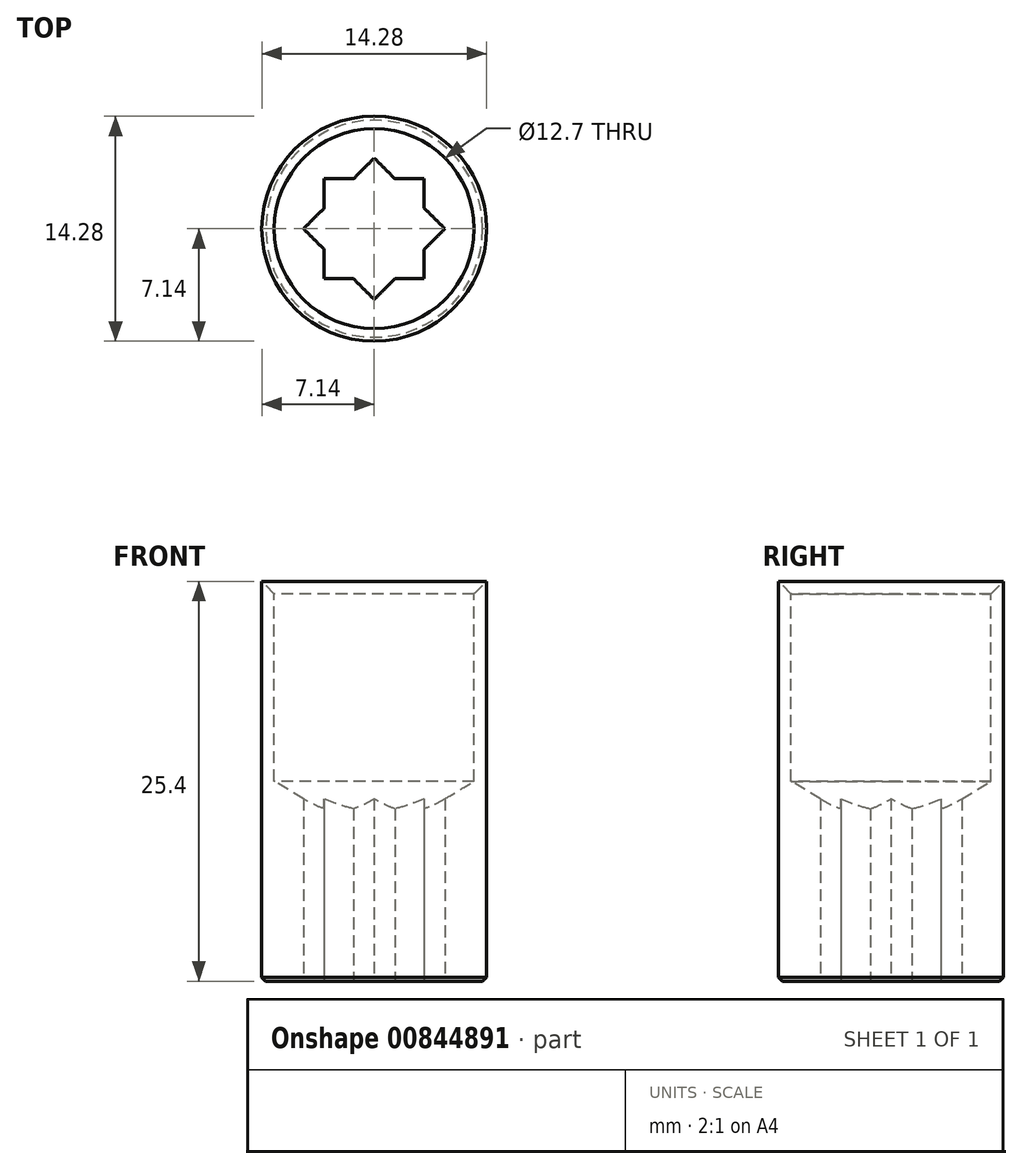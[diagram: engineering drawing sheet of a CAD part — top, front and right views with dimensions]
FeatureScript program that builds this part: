
annotation { "Feature Type Name" : "Feature", "Feature Type Description" : "" }
export const myFeature = defineFeature(function(context is Context, id is Id, definition is map)
    precondition{}
    {
        {
            var Q0;
            Q0=qCreatedBy(makeId("Front.planeOp"),FACE);
            var sketch = newSketch(context, id + "F0", { "sketchPlane" : qUnion([Q0])});
            skLineSegment(sketch, "E0.bottom", {"start": v(0, 0) * mm, "end": v(-7.14, 0) * mm});
            skLineSegment(sketch, "E0.top", {"start": v(0, -25.4) * mm, "end": v(-7.14, -25.4) * mm});
            skLineSegment(sketch, "E0.left", {"start": v(0, 0) * mm, "end": v(0, -25.4) * mm});
            skLineSegment(sketch, "E0.right", {"start": v(-7.14, 0) * mm, "end": v(-7.14, -25.4) * mm});
            skSolve(sketch);
        }
        {
            var Q0;
            Q0=makeQuery(id+"F0.imprint","IMPRINT",FACE,{"disambiguationData":[TD([[makeQuery(id+"F0.imprint","IMPRINT",EDGE,{"derivedFrom":sQuery(id+"F0.wireOp",EDGE,"E0.bottom")}),1.0]])]});
            var Q1;
            Q1=sQuery(id+"F0.wireOp",EDGE,"E0.left");
            revolve(context, id + "F1", {"surfaceOperationType" : NewSurfaceOperationType.NEW, "entities" : qUnion([Q0]), "axis" : qUnion([Q1]), "revolveType" : RevolveType.FULL});
        }
        {
            var Q0;
            Q0=makeQuery(id+"F1.opRevolve","SWEPT_FACE",FACE,{"disambiguationData":[OSD([sQuery(id+"F0.wireOp",EDGE,"E0.bottom")])]});
            var sketch = newSketch(context, id + "F2", { "sketchPlane" : qUnion([Q0])});
            skPoint(sketch, "E1", {"position": v(0, 0) * mm});
            skSolve(sketch);
        }
        {
            var Q0;
            Q0=sQuery(id+"F2.wireOp",VERTEX,"E1");
            var Q1;
            Q1=makeQuery(id+"F1.opRevolve","SWEPT_BODY",BODY,{"disambiguationData":[OSD([sQuery(id+"F0.wireOp",EDGE,"E0.bottom"),sQuery(id+"F0.wireOp",EDGE,"E0.top"),sQuery(id+"F0.wireOp",EDGE,"E0.left"),sQuery(id+"F0.wireOp",EDGE,"E0.right")])]});
            hole(context, id + "F3", {"style" : HoleStyle.C_SINK, "endStyle" : HoleEndStyle.BLIND, "holeDiameter" : 12.7 * mm, "cSinkDiameter" : 14.29 * mm, "cSinkAngle" : 90 * degree, "majorDiameter" : 6.35 * mm, "holeDepth" : 12.7 * mm, "isTappedThrough" : true, "tappedDepth" : 12.7 * mm, "tapClearance" : 3, "locations" : qUnion([Q0]), "scope" : qUnion([Q1])});
        }
        {
            var Q0;
            Q0=makeQuery(id+"F1.opRevolve","SWEPT_FACE",FACE,{"disambiguationData":[OSD([sQuery(id+"F0.wireOp",EDGE,"E0.top")])]});
            var sketch = newSketch(context, id + "F4", { "sketchPlane" : qUnion([Q0])});
            skLineSegment(sketch, "E2.bottom", {"start": v(-3.17, -3.18) * mm, "end": v(3.17, -3.18) * mm});
            skLineSegment(sketch, "E2.top", {"start": v(-3.17, 3.18) * mm, "end": v(3.17, 3.18) * mm});
            skLineSegment(sketch, "E2.left", {"start": v(-3.18, -3.17) * mm, "end": v(-3.18, 3.17) * mm});
            skLineSegment(sketch, "E2.right", {"start": v(3.18, -3.17) * mm, "end": v(3.18, 3.17) * mm});
            skPoint(sketch, "E2.middle", {"position": v(0, 0) * mm});
            skLineSegment(sketch, "E3.bottom", {"start": v(-4.5, 0) * mm, "end": v(0, -4.5) * mm});
            skLineSegment(sketch, "E3.top", {"start": v(0, 4.5) * mm, "end": v(4.5, 0) * mm});
            skLineSegment(sketch, "E3.left", {"start": v(-4.5, 0) * mm, "end": v(0, 4.5) * mm});
            skLineSegment(sketch, "E3.right", {"start": v(0, -4.5) * mm, "end": v(4.5, 0) * mm});
            skSolve(sketch);
        }
        {
            var Q0;
            {var subQ0=sQuery(id+"F4.wireOp",EDGE,"E2.left");var subQ1=sQuery(id+"F4.wireOp",EDGE,"E2.bottom");var subQ2=makeQuery(id+"F4.imprint","INTERSECT",VERTEX,{"derivedFrom":[subQ1,subQ0]});Q0=makeQuery(id+"F4.imprint","IMPRINT",FACE,{"disambiguationData":[TD([[makeQuery(id+"F4.imprint","IMPRINT",EDGE,{"disambiguationData":[TD([[subQ2,-1.0]])],"derivedFrom":subQ1}),1.0]])]});}
            var Q1;
            {var subQ0=sQuery(id+"F4.wireOp",EDGE,"E3.bottom");var subQ1=sQuery(id+"F4.wireOp",EDGE,"E2.bottom");var subQ2=makeQuery(id+"F4.imprint","INTERSECT",VERTEX,{"derivedFrom":[subQ1,subQ0]});Q1=makeQuery(id+"F4.imprint","IMPRINT",FACE,{"disambiguationData":[TD([[makeQuery(id+"F4.imprint","IMPRINT",EDGE,{"disambiguationData":[TD([[subQ2,-1.0]])],"derivedFrom":subQ1}),-1.0]])]});}
            var Q2;
            {var subQ0=sQuery(id+"F4.wireOp",EDGE,"E2.right");var subQ1=sQuery(id+"F4.wireOp",EDGE,"E2.bottom");var subQ2=makeQuery(id+"F4.imprint","INTERSECT",VERTEX,{"derivedFrom":[subQ1,subQ0]});Q2=makeQuery(id+"F4.imprint","IMPRINT",FACE,{"disambiguationData":[TD([[makeQuery(id+"F4.imprint","IMPRINT",EDGE,{"disambiguationData":[TD([[subQ2,1.0]])],"derivedFrom":subQ1}),1.0]])]});}
            var Q3;
            {var subQ0=sQuery(id+"F4.wireOp",EDGE,"E2.left");var subQ1=sQuery(id+"F4.wireOp",EDGE,"E2.top");var subQ2=makeQuery(id+"F4.imprint","INTERSECT",VERTEX,{"derivedFrom":[subQ1,subQ0]});Q3=makeQuery(id+"F4.imprint","IMPRINT",FACE,{"disambiguationData":[TD([[makeQuery(id+"F4.imprint","IMPRINT",EDGE,{"disambiguationData":[TD([[subQ2,-1.0]])],"derivedFrom":subQ1}),-1.0]])]});}
            var Q4;
            {var subQ0=sQuery(id+"F4.wireOp",EDGE,"E3.left");var subQ1=sQuery(id+"F4.wireOp",EDGE,"E2.top");var subQ2=makeQuery(id+"F4.imprint","INTERSECT",VERTEX,{"derivedFrom":[subQ1,subQ0]});Q4=makeQuery(id+"F4.imprint","IMPRINT",FACE,{"disambiguationData":[TD([[makeQuery(id+"F4.imprint","IMPRINT",EDGE,{"disambiguationData":[TD([[subQ2,-1.0]])],"derivedFrom":subQ1}),1.0]])]});}
            var Q5;
            {var subQ0=sQuery(id+"F4.wireOp",EDGE,"E2.right");var subQ1=sQuery(id+"F4.wireOp",EDGE,"E2.top");var subQ2=makeQuery(id+"F4.imprint","INTERSECT",VERTEX,{"derivedFrom":[subQ1,subQ0]});Q5=makeQuery(id+"F4.imprint","IMPRINT",FACE,{"disambiguationData":[TD([[makeQuery(id+"F4.imprint","IMPRINT",EDGE,{"disambiguationData":[TD([[subQ2,1.0]])],"derivedFrom":subQ1}),-1.0]])]});}
            var Q6;
            {var subQ0=sQuery(id+"F4.wireOp",EDGE,"E3.bottom");var subQ1=sQuery(id+"F4.wireOp",EDGE,"E2.left");var subQ2=makeQuery(id+"F4.imprint","INTERSECT",VERTEX,{"derivedFrom":[subQ1,subQ0]});Q6=makeQuery(id+"F4.imprint","IMPRINT",FACE,{"disambiguationData":[TD([[makeQuery(id+"F4.imprint","IMPRINT",EDGE,{"disambiguationData":[TD([[subQ2,-1.0]])],"derivedFrom":subQ1}),1.0]])]});}
            var Q7;
            {var subQ5=sQuery(id+"F4.wireOp",EDGE,"E3.bottom");var subQ13=sQuery(id+"F4.wireOp",EDGE,"E2.bottom");var subQ14=makeQuery(id+"F4.imprint","INTERSECT",VERTEX,{"derivedFrom":[subQ13,subQ5]});Q7=makeQuery(id+"F4.imprint","IMPRINT",FACE,{"disambiguationData":[TD([[makeQuery(id+"F4.imprint","IMPRINT",EDGE,{"disambiguationData":[TD([[subQ14,-1.0]])],"derivedFrom":subQ13}),1.0]])]});}
            var Q8;
            {var subQ0=sQuery(id+"F4.wireOp",EDGE,"E3.right");var subQ1=sQuery(id+"F4.wireOp",EDGE,"E2.right");var subQ2=makeQuery(id+"F4.imprint","INTERSECT",VERTEX,{"derivedFrom":[subQ1,subQ0]});Q8=makeQuery(id+"F4.imprint","IMPRINT",FACE,{"disambiguationData":[TD([[makeQuery(id+"F4.imprint","IMPRINT",EDGE,{"disambiguationData":[TD([[subQ2,-1.0]])],"derivedFrom":subQ1}),-1.0]])]});}
            extrude(context, id + "F5", {"entities" : qUnion([Q0, Q1, Q2, Q3, Q4, Q5, Q6, Q7, Q8]), "operationType" : NewBodyOperationType.REMOVE, "oppositeDirection" : true, "depth" : 12.7 * mm, "offsetDistance" : 25.4 * mm});
        }
        {
            var Q0;
            Q0=makeQuery(id+"F1.opRevolve","SWEPT_EDGE",EDGE,{"disambiguationData":[OSD([sQuery(id+"F0.wireOp",EDGE,"E0.top"),sQuery(id+"F0.wireOp",EDGE,"E0.right")])]});
            chamfer(context, id + "F6", {"entities" : qUnion([Q0]), "width" : 0.25 * mm, "tangentPropagation" : true});
        }
    });
